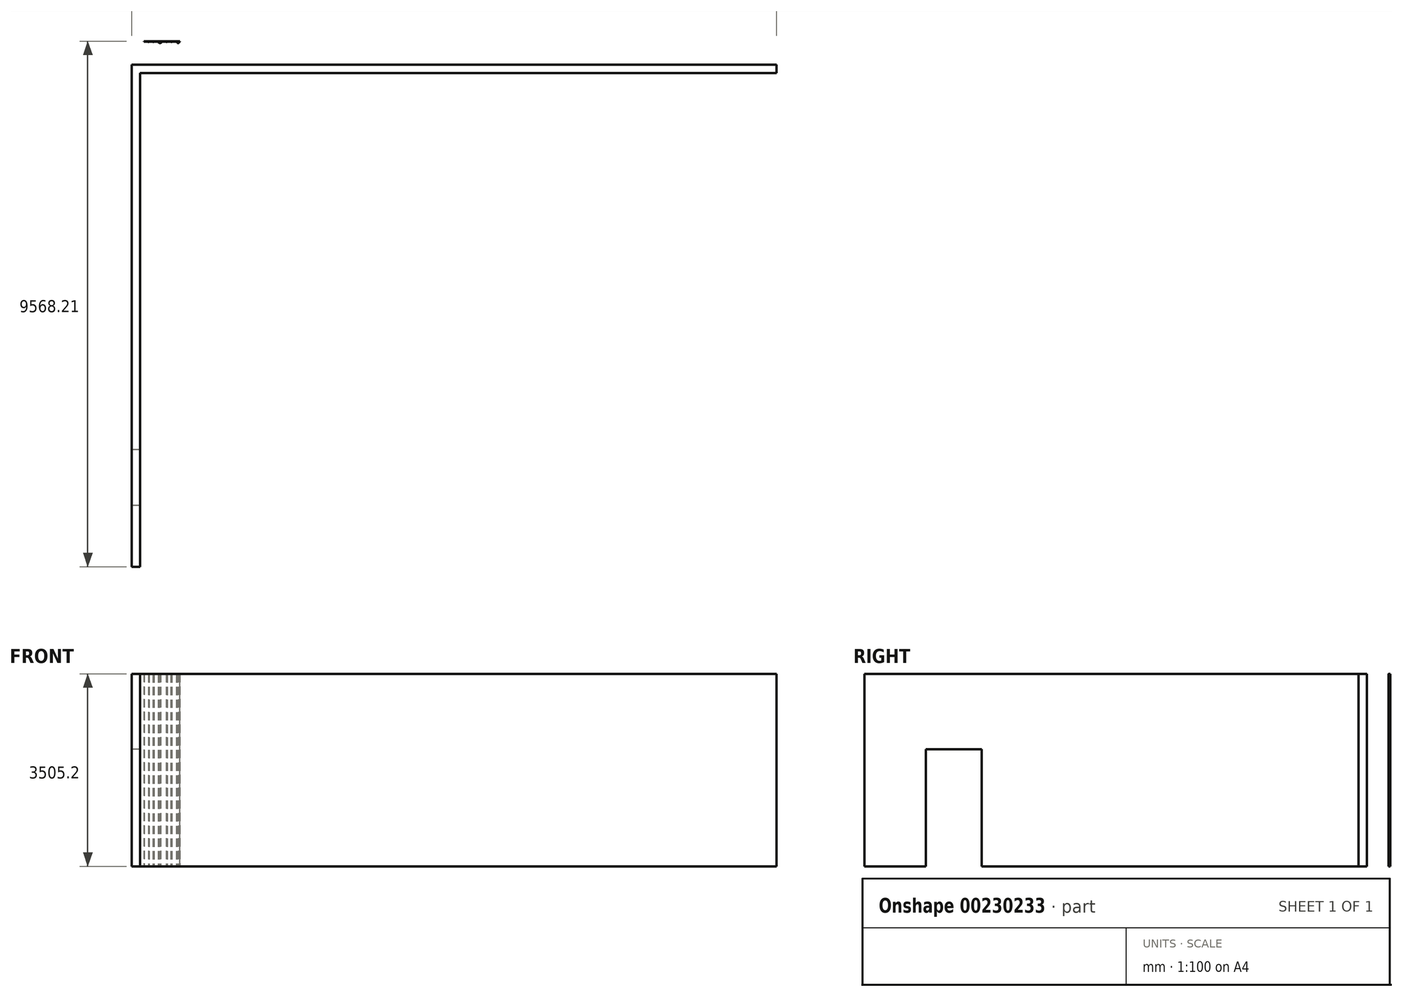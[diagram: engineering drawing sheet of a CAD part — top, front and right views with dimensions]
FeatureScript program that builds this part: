
annotation { "Feature Type Name" : "Feature", "Feature Type Description" : "" }
export const myFeature = defineFeature(function(context is Context, id is Id, definition is map)
    precondition{}
    {
        {
            var Q0;
            Q0=qCreatedBy(makeId("Top.planeOp"),FACE);
            var sketch = newSketch(context, id + "F0", { "sketchPlane" : qUnion([Q0])});
            skLineSegment(sketch, "E0.bottom", {"start": v(0, 0) * mm, "end": v(152.4, 0) * mm});
            skLineSegment(sketch, "E0.top", {"start": v(0, 9144) * mm, "end": v(152.4, 9144) * mm});
            skLineSegment(sketch, "E0.left", {"start": v(0, 0) * mm, "end": v(0, 9144) * mm});
            skLineSegment(sketch, "E0.right", {"start": v(152.4, 0) * mm, "end": v(152.4, 8991.6) * mm});
            skLineSegment(sketch, "E1.bottom", {"start": v(0, 9144) * mm, "end": v(11734.8, 9144) * mm});
            skLineSegment(sketch, "E1.top", {"start": v(152.4, 8991.6) * mm, "end": v(11734.8, 8991.6) * mm});
            skLineSegment(sketch, "E1.left", {"start": v(0, 9144) * mm, "end": v(0, 8991.6) * mm});
            skLineSegment(sketch, "E1.right", {"start": v(11734.8, 9144) * mm, "end": v(11734.8, 8991.6) * mm});
            skSolve(sketch);
        }
        {
            var Q0;
            Q0=qSketchRegion(id+"F0",true);
            extrude(context, id + "F1", {"entities" : qUnion([Q0]), "depth" : 3505.2 * mm});
        }
        {
            var Q0;
            Q0=makeQuery(id+"F1.opExtrude","SWEPT_FACE",FACE,{"disambiguationData":[OSD([sQuery(id+"F0.wireOp",EDGE,"E0.left"),sQuery(id+"F0.wireOp",EDGE,"E1.left")])]});
            var sketch = newSketch(context, id + "F2", { "sketchPlane" : qUnion([Q0])});
            skLineSegment(sketch, "E2", {"start": v(-9144, 0) * mm, "end": v(-2133.6, 0) * mm});
            skLineSegment(sketch, "E3", {"start": v(-2133.6, 0) * mm, "end": v(-2133.6, 2133.6) * mm});
            skLineSegment(sketch, "E4", {"start": v(-2133.6, 2133.6) * mm, "end": v(-1117.6, 2133.6) * mm});
            skLineSegment(sketch, "E5", {"start": v(-1117.6, 2133.6) * mm, "end": v(-1117.6, 0) * mm});
            skLineSegment(sketch, "E6", {"start": v(-1117.6, 0) * mm, "end": v(-2133.6, 0) * mm});
            skSolve(sketch);
        }
        {
            var Q0;
            Q0=qSketchRegion(id+"F2",true);
            extrude(context, id + "F3", {"entities" : qUnion([Q0]), "operationType" : NewBodyOperationType.REMOVE, "oppositeDirection" : true, "depth" : 203.2 * mm});
        }
        {
            var Q0;
            Q0=qCreatedBy(makeId("Top.planeOp"),FACE);
            var sketch = newSketch(context, id + "F4", { "sketchPlane" : qUnion([Q0])});
            skLineSegment(sketch, "E7", {"start": v(221.45, 9561.86) * mm, "end": v(291.3, 9561.86) * mm});
            skLineSegment(sketch, "E8", {"start": v(551.65, 9561.86) * mm, "end": v(621.5, 9561.86) * mm});
            skLineSegment(sketch, "E9", {"start": v(851.57, 9537.39) * mm, "end": v(831.43, 9537.39) * mm});
            skLineSegment(sketch, "E10", {"start": v(524.93, 9536.46) * mm, "end": v(502.16, 9536.46) * mm});
            skLineSegment(sketch, "E11", {"start": v(499.92, 9537.39) * mm, "end": v(475.45, 9561.86) * mm});
            skLineSegment(sketch, "E12", {"start": v(527.18, 9537.39) * mm, "end": v(551.65, 9561.86) * mm});
            skLineSegment(sketch, "E13", {"start": v(829.19, 9538.32) * mm, "end": v(805.65, 9561.86) * mm});
            skLineSegment(sketch, "E14", {"start": v(853.82, 9538.32) * mm, "end": v(877.36, 9561.86) * mm});
            skLineSegment(sketch, "E15", {"start": v(805.65, 9561.86) * mm, "end": v(731.3, 9561.86) * mm});
            skLineSegment(sketch, "E16", {"start": v(710.4, 9561.86) * mm, "end": v(646.9, 9561.86) * mm});
            skLineSegment(sketch, "E17", {"start": v(475.45, 9561.86) * mm, "end": v(405.6, 9561.86) * mm});
            skLineSegment(sketch, "E18", {"start": v(380.2, 9561.86) * mm, "end": v(316.7, 9561.86) * mm});
            skLineSegment(sketch, "E19", {"start": v(298.96, 9555.5) * mm, "end": v(309.03, 9555.5) * mm});
            skLineSegment(sketch, "E20", {"start": v(397.93, 9555.5) * mm, "end": v(387.86, 9555.5) * mm});
            skLineSegment(sketch, "E21", {"start": v(639.23, 9555.5) * mm, "end": v(629.16, 9555.5) * mm});
            skLineSegment(sketch, "E22", {"start": v(724.57, 9556.44) * mm, "end": v(717.13, 9556.44) * mm});
            skLineSegment(sketch, "E23", {"start": v(731.3, 9561.86) * mm, "end": v(726.82, 9557.37) * mm});
            skLineSegment(sketch, "E24", {"start": v(710.4, 9561.86) * mm, "end": v(714.89, 9557.37) * mm});
            skLineSegment(sketch, "E25", {"start": v(646.9, 9561.86) * mm, "end": v(641.48, 9556.44) * mm});
            skLineSegment(sketch, "E26", {"start": v(621.5, 9561.86) * mm, "end": v(626.92, 9556.44) * mm});
            skLineSegment(sketch, "E27", {"start": v(405.6, 9561.86) * mm, "end": v(400.18, 9556.44) * mm});
            skLineSegment(sketch, "E28", {"start": v(380.2, 9561.86) * mm, "end": v(385.62, 9556.44) * mm});
            skLineSegment(sketch, "E29", {"start": v(316.7, 9561.86) * mm, "end": v(311.28, 9556.44) * mm});
            skLineSegment(sketch, "E30", {"start": v(291.3, 9561.86) * mm, "end": v(296.72, 9556.44) * mm});
            skLineSegment(sketch, "E31", {"start": v(221.45, 9561.86) * mm, "end": v(221.45, 9568.2) * mm});
            skLineSegment(sketch, "E32", {"start": v(221.45, 9568.2) * mm, "end": v(877.36, 9568.2) * mm});
            skLineSegment(sketch, "E33", {"start": v(877.36, 9568.2) * mm, "end": v(877.36, 9561.86) * mm});
            skLineSegment(sketch, "E34.trimOffspring", {"start": v(731.3, 9561.86) * mm, "end": v(805.65, 9561.86) * mm});
            skLineSegment(sketch, "E35.trimOffspring", {"start": v(646.9, 9561.86) * mm, "end": v(710.4, 9561.86) * mm});
            skLineSegment(sketch, "E36.trimOffspring", {"start": v(405.6, 9561.86) * mm, "end": v(475.45, 9561.86) * mm});
            skLineSegment(sketch, "E37.trimOffspring", {"start": v(316.7, 9561.86) * mm, "end": v(380.2, 9561.86) * mm});
            skPoint(sketch, "E38.visualSharp", {"position": v(852.89, 9537.39) * mm});
            skArc(sketch, "E38.filletArc", {"start": v(851.57, 9537.39) * mm, "mid": v(852.79, 9537.63) * mm, "end": v(853.82, 9538.32) * mm});
            skPoint(sketch, "E39.visualSharp", {"position": v(830.12, 9537.39) * mm});
            skArc(sketch, "E39.filletArc", {"start": v(829.19, 9538.32) * mm, "mid": v(830.22, 9537.63) * mm, "end": v(831.43, 9537.39) * mm});
            skPoint(sketch, "E40.visualSharp", {"position": v(725.89, 9556.44) * mm});
            skArc(sketch, "E40.filletArc", {"start": v(724.57, 9556.44) * mm, "mid": v(725.79, 9556.68) * mm, "end": v(726.82, 9557.37) * mm});
            skPoint(sketch, "E41.visualSharp", {"position": v(715.82, 9556.44) * mm});
            skArc(sketch, "E41.filletArc", {"start": v(714.89, 9557.37) * mm, "mid": v(715.92, 9556.68) * mm, "end": v(717.13, 9556.44) * mm});
            skPoint(sketch, "E42.visualSharp", {"position": v(640.55, 9555.5) * mm});
            skArc(sketch, "E42.filletArc", {"start": v(639.23, 9555.5) * mm, "mid": v(640.45, 9555.75) * mm, "end": v(641.48, 9556.44) * mm});
            skPoint(sketch, "E43.visualSharp", {"position": v(627.85, 9555.5) * mm});
            skArc(sketch, "E43.filletArc", {"start": v(626.92, 9556.44) * mm, "mid": v(627.95, 9555.75) * mm, "end": v(629.16, 9555.5) * mm});
            skPoint(sketch, "E44.visualSharp", {"position": v(526.25, 9536.46) * mm});
            skArc(sketch, "E44.filletArc", {"start": v(524.93, 9536.46) * mm, "mid": v(526.15, 9536.7) * mm, "end": v(527.18, 9537.39) * mm});
            skPoint(sketch, "E45.visualSharp", {"position": v(500.85, 9536.46) * mm});
            skArc(sketch, "E45.filletArc", {"start": v(499.92, 9537.39) * mm, "mid": v(500.95, 9536.7) * mm, "end": v(502.16, 9536.46) * mm});
            skPoint(sketch, "E46.visualSharp", {"position": v(399.25, 9555.5) * mm});
            skArc(sketch, "E46.filletArc", {"start": v(397.93, 9555.5) * mm, "mid": v(399.15, 9555.75) * mm, "end": v(400.18, 9556.44) * mm});
            skPoint(sketch, "E47.visualSharp", {"position": v(386.55, 9555.5) * mm});
            skArc(sketch, "E47.filletArc", {"start": v(385.62, 9556.44) * mm, "mid": v(386.65, 9555.75) * mm, "end": v(387.86, 9555.5) * mm});
            skPoint(sketch, "E48.visualSharp", {"position": v(310.35, 9555.5) * mm});
            skArc(sketch, "E48.filletArc", {"start": v(309.03, 9555.5) * mm, "mid": v(310.25, 9555.75) * mm, "end": v(311.28, 9556.44) * mm});
            skPoint(sketch, "E49.visualSharp", {"position": v(297.65, 9555.5) * mm});
            skArc(sketch, "E49.filletArc", {"start": v(296.72, 9556.44) * mm, "mid": v(297.75, 9555.75) * mm, "end": v(298.96, 9555.5) * mm});
            skSolve(sketch);
        }
        {
            var Q0;
            Q0=makeQuery(id+"F4.imprint","IMPRINT",FACE,{"disambiguationData":[TD([[makeQuery(id+"F4.imprint","IMPRINT",EDGE,{"derivedFrom":sQuery(id+"F4.wireOp",EDGE,"E7")}),1.0]])]});
            extrude(context, id + "F5", {"entities" : qUnion([Q0]), "depth" : 3505.2 * mm});
        }
        {
            var Q0;
            Q0=makeQuery(id+"F5.opExtrude","SWEPT_FACE",FACE,{"disambiguationData":[OSD([sQuery(id+"F4.wireOp",EDGE,"E32")])]});
            shell(context, id + "F6", {"entities" : qUnion([Q0]), "thickness" : 4.78 * mm});
        }
        {
            var Q0;
            Q0=makeQuery(id+"F5.opExtrude","SWEPT_EDGE",EDGE,{"disambiguationData":[OSD([sQuery(id+"F4.wireOp",EDGE,"E13"),sQuery(id+"F4.wireOp",EDGE,"E34.trimOffspring")])]});
            var Q1;
            Q1=makeQuery(id+"F5.opExtrude","SWEPT_EDGE",EDGE,{"disambiguationData":[OSD([sQuery(id+"F4.wireOp",EDGE,"E23"),sQuery(id+"F4.wireOp",EDGE,"E34.trimOffspring")])]});
            var Q2;
            Q2=makeQuery(id+"F5.opExtrude","SWEPT_EDGE",EDGE,{"disambiguationData":[OSD([sQuery(id+"F4.wireOp",EDGE,"E24"),sQuery(id+"F4.wireOp",EDGE,"E35.trimOffspring")])]});
            var Q3;
            Q3=makeQuery(id+"F5.opExtrude","SWEPT_EDGE",EDGE,{"disambiguationData":[OSD([sQuery(id+"F4.wireOp",EDGE,"E25"),sQuery(id+"F4.wireOp",EDGE,"E35.trimOffspring")])]});
            var Q4;
            Q4=makeQuery(id+"F5.opExtrude","SWEPT_EDGE",EDGE,{"disambiguationData":[OSD([sQuery(id+"F4.wireOp",EDGE,"E8"),sQuery(id+"F4.wireOp",EDGE,"E26")])]});
            var Q5;
            Q5=makeQuery(id+"F5.opExtrude","SWEPT_EDGE",EDGE,{"disambiguationData":[OSD([sQuery(id+"F4.wireOp",EDGE,"E8"),sQuery(id+"F4.wireOp",EDGE,"E12")])]});
            var Q6;
            Q6=makeQuery(id+"F5.opExtrude","SWEPT_EDGE",EDGE,{"disambiguationData":[OSD([sQuery(id+"F4.wireOp",EDGE,"E11"),sQuery(id+"F4.wireOp",EDGE,"E36.trimOffspring")])]});
            var Q7;
            Q7=makeQuery(id+"F5.opExtrude","SWEPT_EDGE",EDGE,{"disambiguationData":[OSD([sQuery(id+"F4.wireOp",EDGE,"E27"),sQuery(id+"F4.wireOp",EDGE,"E36.trimOffspring")])]});
            var Q8;
            Q8=makeQuery(id+"F5.opExtrude","SWEPT_EDGE",EDGE,{"disambiguationData":[OSD([sQuery(id+"F4.wireOp",EDGE,"E28"),sQuery(id+"F4.wireOp",EDGE,"E37.trimOffspring")])]});
            var Q9;
            Q9=makeQuery(id+"F5.opExtrude","SWEPT_EDGE",EDGE,{"disambiguationData":[OSD([sQuery(id+"F4.wireOp",EDGE,"E29"),sQuery(id+"F4.wireOp",EDGE,"E37.trimOffspring")])]});
            var Q10;
            Q10=makeQuery(id+"F5.opExtrude","SWEPT_EDGE",EDGE,{"disambiguationData":[OSD([sQuery(id+"F4.wireOp",EDGE,"E7"),sQuery(id+"F4.wireOp",EDGE,"E30")])]});
            fillet(context, id + "F7", {"entities" : qUnion([Q0, Q1, Q2, Q3, Q4, Q5, Q6, Q7, Q8, Q9, Q10]), "radius" : 3.17 * mm, "tangentPropagation" : true, "allowEdgeOverflow" : false});
        }
        {
            var Q0;
            Q0=makeQuery(id+"F6.opShell","OFFSET_EDGE",EDGE,{"disambiguationData":[OSD([sQuery(id+"F4.wireOp",EDGE,"E29"),sQuery(id+"F4.wireOp",EDGE,"E37.trimOffspring")])]});
            var Q1;
            Q1=makeQuery(id+"F6.opShell","OFFSET_EDGE",EDGE,{"disambiguationData":[OSD([sQuery(id+"F4.wireOp",EDGE,"E7"),sQuery(id+"F4.wireOp",EDGE,"E30")])]});
            var Q2;
            Q2=makeQuery(id+"F6.opShell","OFFSET_EDGE",EDGE,{"disambiguationData":[OSD([sQuery(id+"F4.wireOp",EDGE,"E28"),sQuery(id+"F4.wireOp",EDGE,"E37.trimOffspring")])]});
            var Q3;
            Q3=makeQuery(id+"F6.opShell","OFFSET_EDGE",EDGE,{"disambiguationData":[OSD([sQuery(id+"F4.wireOp",EDGE,"E27"),sQuery(id+"F4.wireOp",EDGE,"E36.trimOffspring")])]});
            var Q4;
            Q4=makeQuery(id+"F6.opShell","OFFSET_EDGE",EDGE,{"disambiguationData":[OSD([sQuery(id+"F4.wireOp",EDGE,"E11"),sQuery(id+"F4.wireOp",EDGE,"E36.trimOffspring")])]});
            var Q5;
            Q5=makeQuery(id+"F6.opShell","OFFSET_EDGE",EDGE,{"disambiguationData":[OSD([sQuery(id+"F4.wireOp",EDGE,"E8"),sQuery(id+"F4.wireOp",EDGE,"E12")])]});
            var Q6;
            Q6=makeQuery(id+"F6.opShell","OFFSET_EDGE",EDGE,{"disambiguationData":[OSD([sQuery(id+"F4.wireOp",EDGE,"E8"),sQuery(id+"F4.wireOp",EDGE,"E26")])]});
            var Q7;
            Q7=makeQuery(id+"F6.opShell","OFFSET_EDGE",EDGE,{"disambiguationData":[OSD([sQuery(id+"F4.wireOp",EDGE,"E25"),sQuery(id+"F4.wireOp",EDGE,"E35.trimOffspring")])]});
            var Q8;
            Q8=makeQuery(id+"F6.opShell","OFFSET_EDGE",EDGE,{"disambiguationData":[OSD([sQuery(id+"F4.wireOp",EDGE,"E24"),sQuery(id+"F4.wireOp",EDGE,"E35.trimOffspring")])]});
            var Q9;
            Q9=makeQuery(id+"F6.opShell","OFFSET_EDGE",EDGE,{"disambiguationData":[OSD([sQuery(id+"F4.wireOp",EDGE,"E23"),sQuery(id+"F4.wireOp",EDGE,"E34.trimOffspring")])]});
            var Q10;
            Q10=makeQuery(id+"F6.opShell","OFFSET_EDGE",EDGE,{"disambiguationData":[OSD([sQuery(id+"F4.wireOp",EDGE,"E13"),sQuery(id+"F4.wireOp",EDGE,"E34.trimOffspring")])]});
            var Q11;
            Q11=makeQuery(id+"F6.opShell","OFFSET_EDGE",EDGE,{"disambiguationData":[OSD([sQuery(id+"F4.wireOp",EDGE,"E32"),sQuery(id+"F4.wireOp",EDGE,"E33")])]});
            fillet(context, id + "F8", {"entities" : qUnion([Q0, Q1, Q2, Q3, Q4, Q5, Q6, Q7, Q8, Q9, Q10, Q11]), "radius" : 5.08 * mm, "tangentPropagation" : true, "allowEdgeOverflow" : false});
        }
    });
